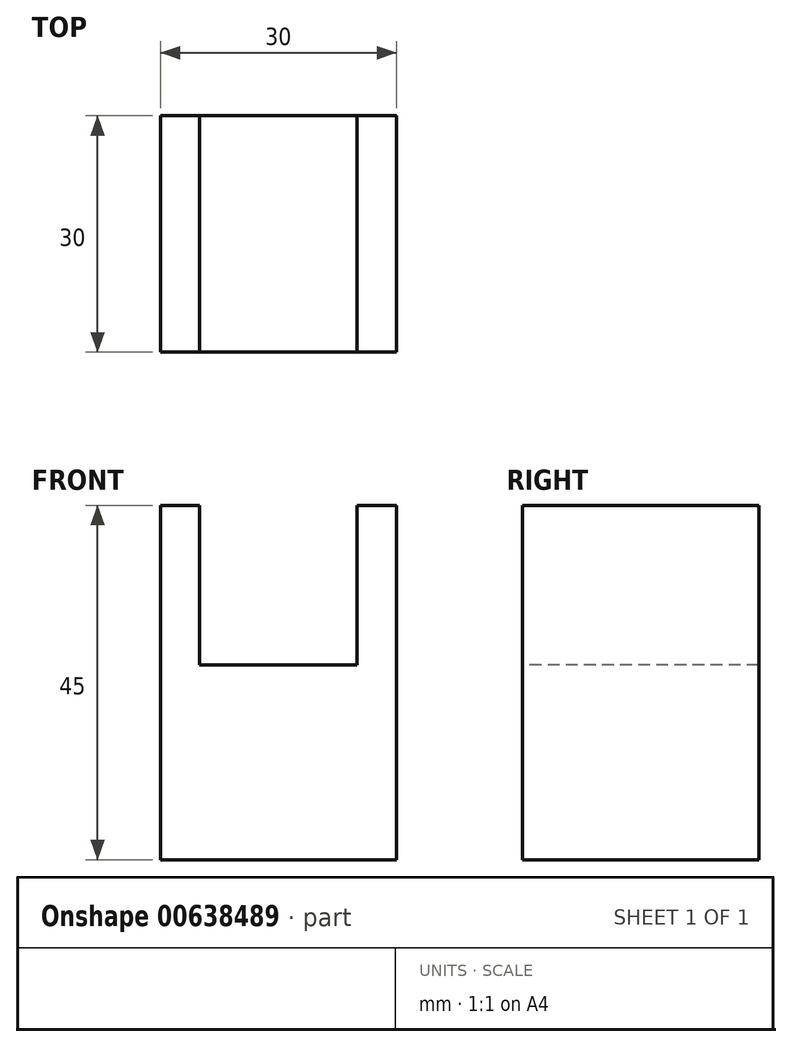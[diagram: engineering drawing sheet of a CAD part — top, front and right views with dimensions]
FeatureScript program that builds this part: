
annotation { "Feature Type Name" : "Feature", "Feature Type Description" : "" }
export const myFeature = defineFeature(function(context is Context, id is Id, definition is map)
    precondition{}
    {
        {
            var Q0;
            Q0=qCreatedBy(makeId("Top.planeOp"),FACE);
            var sketch = newSketch(context, id + "F0", { "sketchPlane" : qUnion([Q0])});
            skLineSegment(sketch, "E0.bottom", {"start": v(15, 15) * mm, "end": v(-15, 15) * mm});
            skLineSegment(sketch, "E0.top", {"start": v(15, -15) * mm, "end": v(-15, -15) * mm});
            skLineSegment(sketch, "E0.left", {"start": v(15, 15) * mm, "end": v(15, -15) * mm});
            skLineSegment(sketch, "E0.right", {"start": v(-15, 15) * mm, "end": v(-15, -15) * mm});
            skPoint(sketch, "E0.middle", {"position": v(0, 0) * mm});
            skSolve(sketch);
        }
        {
            var Q0;
            Q0=makeQuery(id+"F0.imprint","IMPRINT",FACE,{"disambiguationData":[TD([[makeQuery(id+"F0.imprint","IMPRINT",EDGE,{"derivedFrom":sQuery(id+"F0.wireOp",EDGE,"E0.bottom")}),1.0]])]});
            extrude(context, id + "F1", {"entities" : qUnion([Q0]), "depth" : 45 * mm, "offsetDistance" : 25 * mm});
        }
        {
            var Q0;
            Q0=makeQuery(id+"F1.opExtrude","CAP_FACE",FACE,{"disambiguationData":[OSD([sQuery(id+"F0.wireOp",EDGE,"E0.bottom"),sQuery(id+"F0.wireOp",EDGE,"E0.top"),sQuery(id+"F0.wireOp",EDGE,"E0.left"),sQuery(id+"F0.wireOp",EDGE,"E0.right")])],"isStart":false});
            var sketch = newSketch(context, id + "F2", { "sketchPlane" : qUnion([Q0])});
            skLineSegment(sketch, "E1.bottom", {"start": v(10, 19.45) * mm, "end": v(-10, 19.45) * mm});
            skLineSegment(sketch, "E1.top", {"start": v(10, -18.65) * mm, "end": v(-10, -18.65) * mm});
            skLineSegment(sketch, "E1.left", {"start": v(10, 19.45) * mm, "end": v(10, -18.65) * mm});
            skLineSegment(sketch, "E1.right", {"start": v(-10, 19.45) * mm, "end": v(-10, -18.65) * mm});
            skPoint(sketch, "E1.middle", {"position": v(0, 0) * mm});
            skPoint(sketch, "E2", {"position": v(0, -15) * mm});
            skPoint(sketch, "E3", {"position": v(0, -18.65) * mm});
            skSolve(sketch);
        }
        {
            var Q0;
            {var subQ0=sQuery(id+"F2.wireOp",EDGE,"E1.left");var subQ1=makeQuery(id+"F1.opExtrude","CAP_EDGE",EDGE,{"disambiguationData":[OSD([sQuery(id+"F0.wireOp",EDGE,"E0.bottom")])],"isStart":false});var subQ2=makeQuery(id+"F2.imprint","INTERSECT",VERTEX,{"derivedFrom":[subQ1,subQ0]});Q0=makeQuery(id+"F2.imprint","IMPRINT",FACE,{"disambiguationData":[TD([[makeQuery(id+"F2.imprint","IMPRINT",EDGE,{"disambiguationData":[TD([[subQ2,-1.0]])],"derivedFrom":subQ0}),-1.0]])]});}
            extrude(context, id + "F3", {"entities" : qUnion([Q0]), "operationType" : NewBodyOperationType.REMOVE, "oppositeDirection" : true, "depth" : (21 - 0.75) * mm, "offsetDistance" : 25 * mm});
        }
    });
